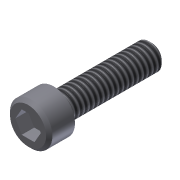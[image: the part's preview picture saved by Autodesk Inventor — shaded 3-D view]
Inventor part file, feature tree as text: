
AUTODESK INVENTOR PART (.ipt)
format: ipt  version: 2013 (Build 170138000, 138)  size: 107,520 bytes
history: native  units: in
note: dims shown in document units (in); Inventor stores cm internally (conversion verified against a paired STEP export)
features: extrude x3, sketch x3, chamfer x2, thread x1
ambient origin geometry x8: Origin, YZ Plane, XZ Plane, XY Plane, X Axis, Y Axis, Z Axis, Center Point
bodies: Solid1 (feature_tree)
feature tree (9):
  extrude  "Extrusion1"  Depth=0.164in TaperAngle=0.0deg
  extrude  "Extrusion2"  Depth=0.625in TaperAngle=0.0deg
  extrude  "Extrusion3"  Depth=0.08in TaperAngle=0.0deg
  thread  "Thread1"  [1 undecoded]
  chamfer  "Chamfer1"  [1 undecoded]
  chamfer  "Chamfer2"  [1 undecoded]
  sketch  "Sketch1"  dims[d0=0.27in d1=0.164in d2=0.0in]
  sketch  "Sketch2"  dims[d3=0.164in d4=0.625in d5=0.0in]
  sketch  "Sketch3"  dims[d6=0.1406in d7=0.08in d8=0.0in d9=1.0in d10=0.0in d11=0.02in d12=0.125in d13=45.0deg d14=0.02in d15=0.125in d16=45.0deg]
note: 3 required parameter values undecoded (feature->parameter linkage not recoverable at this tier; creation-order binding heuristic only, values carry confidence <= 0.55)
